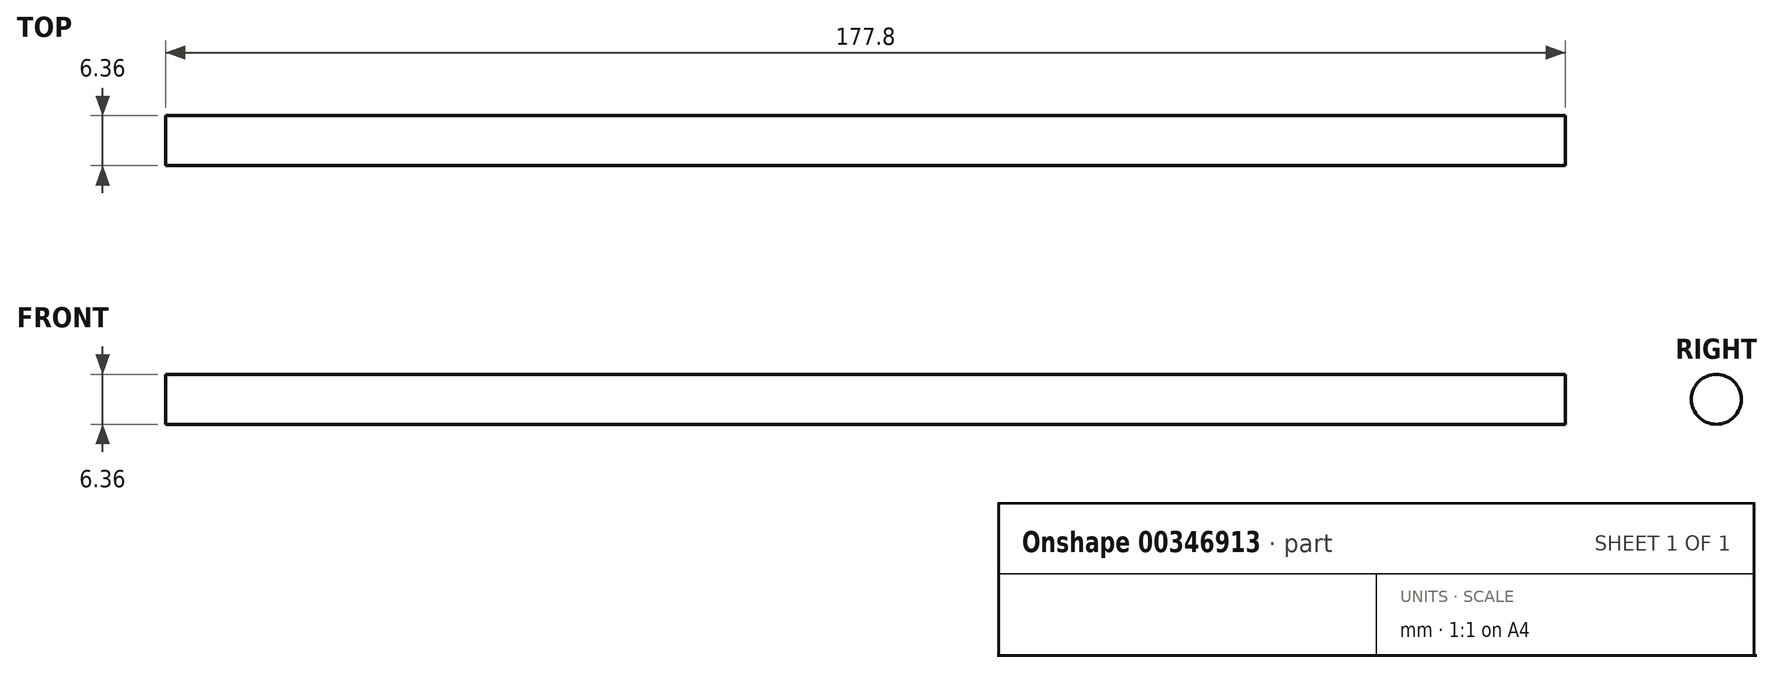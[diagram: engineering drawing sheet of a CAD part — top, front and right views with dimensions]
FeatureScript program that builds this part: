
annotation { "Feature Type Name" : "Feature", "Feature Type Description" : "" }
export const myFeature = defineFeature(function(context is Context, id is Id, definition is map)
    precondition{}
    {
        {
            var Q0;
            Q0=qCreatedBy(makeId("Right.planeOp"),FACE);
            var sketch = newSketch(context, id + "F0", { "sketchPlane" : qUnion([Q0])});
            skCircle(sketch, "E0", {"center": v(0, 0) * mm, "radius": 3.18 * mm});
            skSolve(sketch);
        }
        {
            var Q0;
            Q0=makeQuery(id+"F0.imprint","IMPRINT",FACE,{"disambiguationData":[TD([[makeQuery(id+"F0.imprint","IMPRINT",EDGE,{"derivedFrom":sQuery(id+"F0.wireOp",EDGE,"E0")}),1.0]])]});
            extrude(context, id + "F1", {"entities" : qUnion([Q0]), "depth" : 177.8 * mm});
        }
    });
